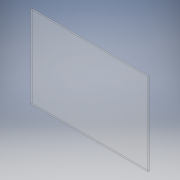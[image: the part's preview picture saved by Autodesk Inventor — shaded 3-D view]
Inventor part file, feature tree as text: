
AUTODESK INVENTOR PART (.ipt)
format: ipt  version: 2017 SP1 (Build 210196100, 196)  size: 94,208 bytes
history: native  units: in
note: dims shown in document units (in); Inventor stores cm internally (conversion verified against a paired STEP export)
features: extrude x1, sketch x1
ambient origin geometry x8: Origin, YZ Plane, XZ Plane, XY Plane, X Axis, Y Axis, Z Axis, Center Point
bodies: Solid1 (feature_tree)
feature tree (2):
  extrude  "Extrusion1"  Depth=7.0in
  sketch  "Sketch1"  dims[d0=10.0in d1=7.0in d2=0.125in d3=0.0in]
